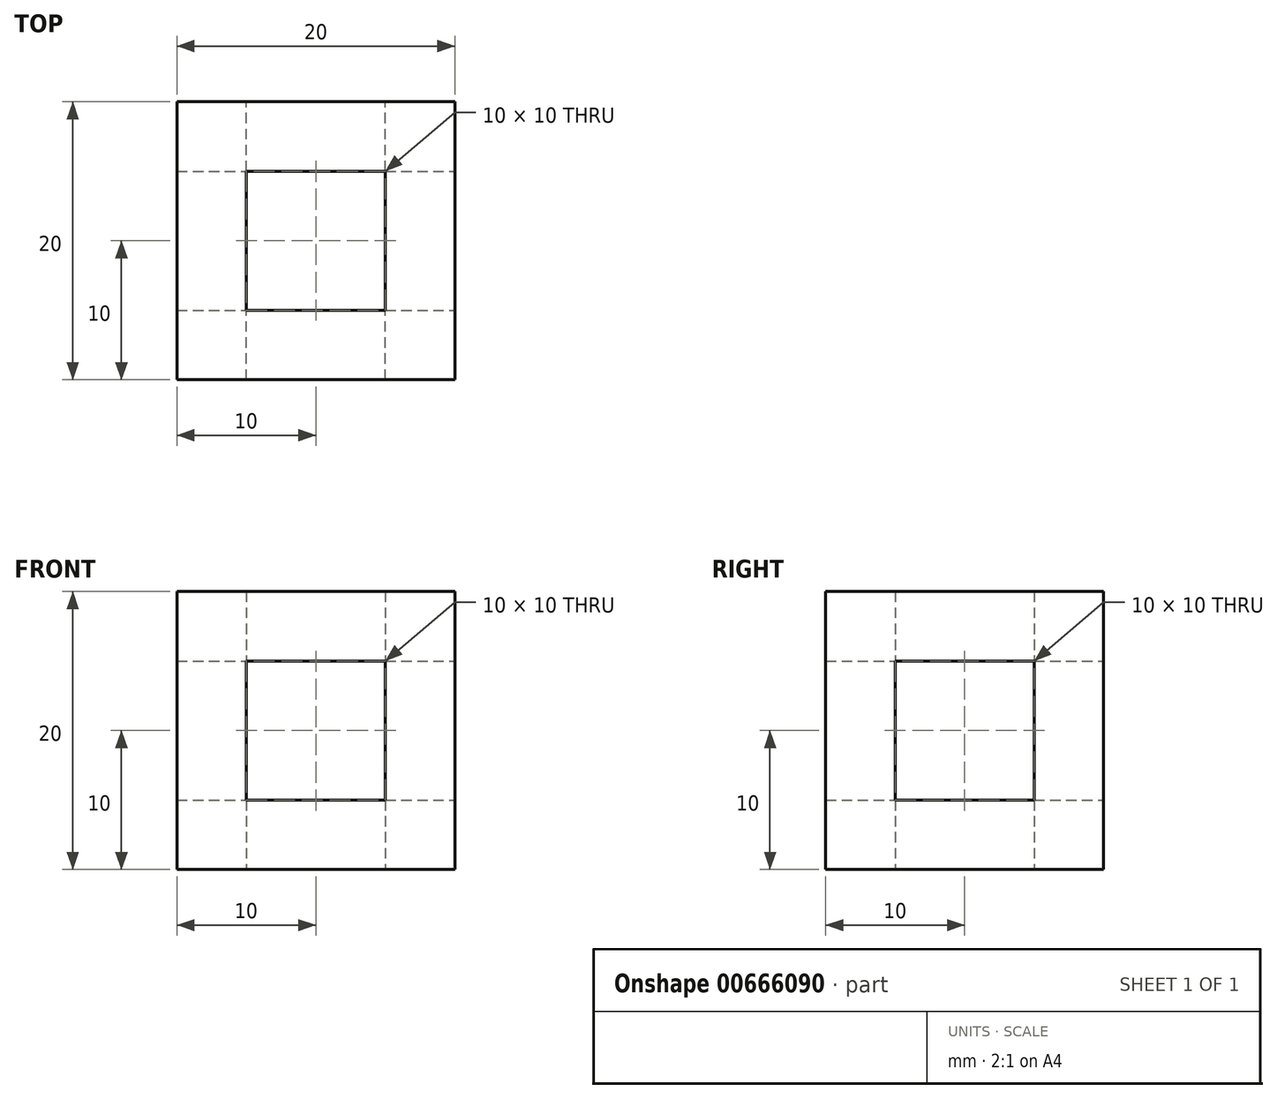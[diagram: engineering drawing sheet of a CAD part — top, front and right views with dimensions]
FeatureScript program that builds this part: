
annotation { "Feature Type Name" : "Feature", "Feature Type Description" : "" }
export const myFeature = defineFeature(function(context is Context, id is Id, definition is map)
    precondition{}
    {
        {
            var Q0;
            Q0=qCreatedBy(makeId("Top.planeOp"),FACE);
            var sketch = newSketch(context, id + "F0", { "sketchPlane" : qUnion([Q0])});
            skLineSegment(sketch, "E0.bottom", {"start": v(0, 0) * mm, "end": v(20, 0) * mm});
            skLineSegment(sketch, "E0.top", {"start": v(0, 20) * mm, "end": v(20, 20) * mm});
            skLineSegment(sketch, "E0.left", {"start": v(0, 0) * mm, "end": v(0, 20) * mm});
            skLineSegment(sketch, "E0.right", {"start": v(20, 0) * mm, "end": v(20, 20) * mm});
            skLineSegment(sketch, "E1.bottom", {"start": v(5, 15) * mm, "end": v(15, 15) * mm});
            skLineSegment(sketch, "E1.top", {"start": v(5, 5) * mm, "end": v(15, 5) * mm});
            skLineSegment(sketch, "E1.left", {"start": v(5, 15) * mm, "end": v(5, 5) * mm});
            skLineSegment(sketch, "E1.right", {"start": v(15, 15) * mm, "end": v(15, 5) * mm});
            skSolve(sketch);
        }
        {
            var Q0;
            Q0 = qSketchRegion(id + "F0", true);
            extrude(context, id + "F1", {"entities" : qUnion([Q0]), "depth" : 20 * mm, "offsetDistance" : 25.4 * mm});
        }
        {
            var Q0;
            Q0=makeQuery(id+"F1.opExtrude","SWEPT_FACE",FACE,{"disambiguationData":[OSD([sQuery(id+"F0.wireOp",EDGE,"E0.right")])]});
            var sketch = newSketch(context, id + "F2", { "sketchPlane" : qUnion([Q0])});
            skLineSegment(sketch, "E2.bottom", {"start": v(15, 15) * mm, "end": v(5, 15) * mm});
            skLineSegment(sketch, "E2.top", {"start": v(15, 5) * mm, "end": v(5, 5) * mm});
            skLineSegment(sketch, "E2.left", {"start": v(15, 15) * mm, "end": v(15, 5) * mm});
            skLineSegment(sketch, "E2.right", {"start": v(5, 15) * mm, "end": v(5, 5) * mm});
            skSolve(sketch);
        }
        {
            var Q0;
            Q0 = qSketchRegion(id + "F2", true);
            extrude(context, id + "F3", {"entities" : qUnion([Q0]), "operationType" : NewBodyOperationType.REMOVE, "endBound" : BoundingType.THROUGH_ALL, "oppositeDirection" : true, "depth" : 25 * mm, "offsetDistance" : 25 * mm});
        }
        {
            var Q0;
            Q0=makeQuery(id+"F1.opExtrude","SWEPT_FACE",FACE,{"disambiguationData":[OSD([sQuery(id+"F0.wireOp",EDGE,"E0.top")])]});
            var sketch = newSketch(context, id + "F4", { "sketchPlane" : qUnion([Q0])});
            skLineSegment(sketch, "E3.bottom", {"start": v(-15, 15) * mm, "end": v(-5, 15) * mm});
            skLineSegment(sketch, "E3.top", {"start": v(-15, 5) * mm, "end": v(-5, 5) * mm});
            skLineSegment(sketch, "E3.left", {"start": v(-15, 15) * mm, "end": v(-15, 5) * mm});
            skLineSegment(sketch, "E3.right", {"start": v(-5, 15) * mm, "end": v(-5, 5) * mm});
            skSolve(sketch);
        }
        {
            var Q0;
            Q0 = qSketchRegion(id + "F4", true);
            extrude(context, id + "F5", {"entities" : qUnion([Q0]), "operationType" : NewBodyOperationType.REMOVE, "endBound" : BoundingType.THROUGH_ALL, "oppositeDirection" : true, "depth" : 25 * mm, "offsetDistance" : 25 * mm});
        }
    });
